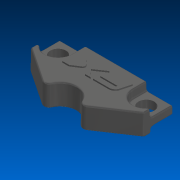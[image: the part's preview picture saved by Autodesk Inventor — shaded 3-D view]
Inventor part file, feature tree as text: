
AUTODESK INVENTOR PART (.ipt)
format: ipt  version: 2022.2 (Build 262287000, 287)  size: 492,544 bytes
history: native  units: in
note: dims shown in document units (in); Inventor stores cm internally (conversion verified against a paired STEP export)
features: fillet x1
ambient origin geometry x8: Origin, YZ Plane, XZ Plane, XY Plane, X Axis, Y Axis, Z Axis, Center Point
bodies: Solid1 (feature_tree)
feature tree (1):
  fillet  "Fillet3"  [1 undecoded]
note: 1 required parameter value undecoded (feature->parameter linkage not recoverable at this tier; creation-order binding heuristic only, values carry confidence <= 0.55)
